# Revit family: Specialty_Equipment-Planter-Planters_Unlimited-Modern-Low_Bowl-bk1
name_source: partatom
category: Specialty Equipment
units: mm (PartAtom-declared; Revit-internal decimal feet)

## family parameters
Always vertical = Yes
Cut with Voids When Loaded = No
OmniClass Number = 23.40.05.21.17
OmniClass Title = Planters
Part Type = Normal
Room Calculation Point = No
Round Connector Dimension = Use Diameter
Shared = No
Work Plane-Based = No

## types (10) — shared parameters
Assembly Code = G2050600
CD_Diameter Max = 6' - 0"
CD_Diameter Min = 1' - 6"
CD_Finish = Plastic-Fiberglass-Carlsbad-Semi_Gloss-Charcoal
CD_Height Max = 1' - 3"
CD_Height Min = 0' - 4"
CD_Microsite = https://www.caddetails.com
CD_Offset = 0' - 0"
CD_Product Page URL = https://www.plantersunlimited.com
CD_Specification = https://www.plantersunlimited.com
Default Elevation = 0' - 0"
Description = Modular Planting Bed
Manufacturer = Planters Unlimited
Model = Modern Series Planters
Type Comments = Modern Fiberglass Low Bowl Planter
URL = https://www.plantersunlimited.com

## per-type parameters (varying)
| type | CD_Base Diameter | CD_Diameter | CD_Height | CD_Requested Diameter | CD_Requested Height |
| 18" Dia x 4"H | 1' - 0" | 1' - 6" | 0' - 4" | 1' - 6" | 0' - 4" |
| 20" Dia x 8"H | 1' - 1" | 1' - 8" | 0' - 8" | 1' - 8" | 0' - 8" |
| 24" Dia x 6"H | 1' - 3" | 2' - 0" | 0' - 6" | 2' - 0" | 0' - 6" |
| 30" Dia x 8"H | 1' - 6" | 2' - 6" | 0' - 8" | 2' - 6" | 0' - 8" |
| 36" Dia x 9"H | 1' - 9" | 3' - 0" | 0' - 9" | 3' - 0" | 0' - 9" |
| 42" Dia x 10"H | 2' - 0" | 3' - 6" | 0' - 10" | 3' - 6" | 0' - 10" |
| 48" Dia x 11"H | 2' - 3" | 4' - 0" | 0' - 11" | 4' - 0" | 0' - 11" |
| 54" Dia x 12"H | 2' - 6" | 4' - 6" | 1' - 0" | 4' - 6" | 1' - 0" |
| 60" Dia x 13"H | 2' - 9" | 5' - 0" | 1' - 1" | 5' - 0" | 1' - 1" |
| 72" Dia x 15"H | 3' - 3" | 6' - 0" | 1' - 3" | 6' - 0" | 1' - 3" |

## geometry (parser evidence)
native form markers: Sweep x2
no freeform markers — native parametric forms only
